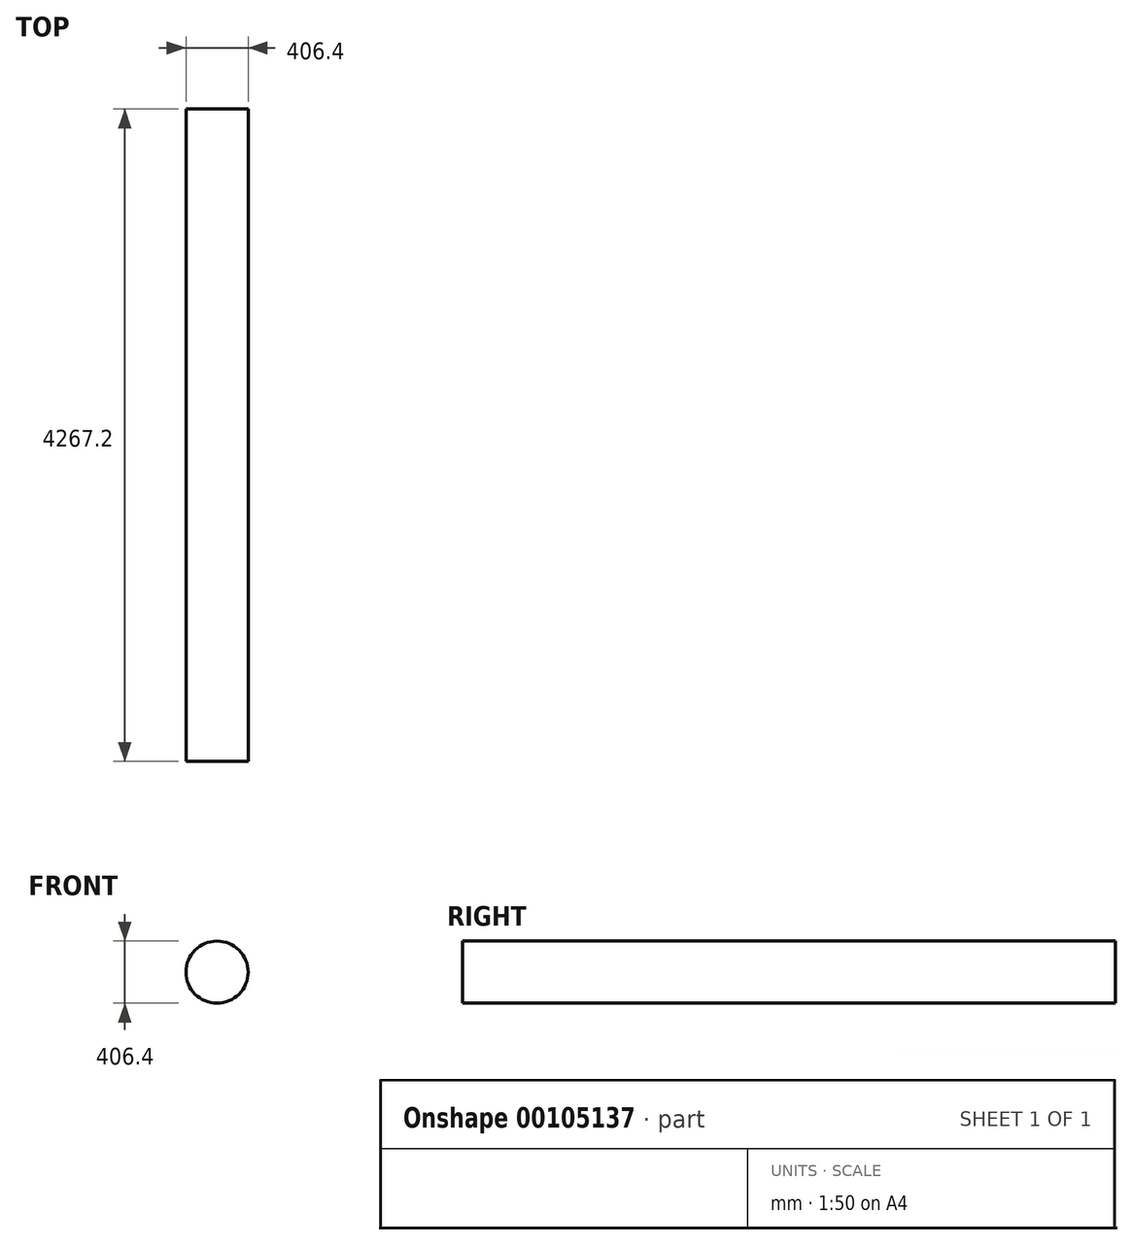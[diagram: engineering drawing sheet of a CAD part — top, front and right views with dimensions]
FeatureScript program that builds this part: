
annotation { "Feature Type Name" : "Feature", "Feature Type Description" : "" }
export const myFeature = defineFeature(function(context is Context, id is Id, definition is map)
    precondition{}
    {
        {
            var Q0;
            Q0=qCreatedBy(makeId("Front.planeOp"),FACE);
            var sketch = newSketch(context, id + "F0", { "sketchPlane" : qUnion([Q0])});
            skCircle(sketch, "E0", {"center": v(0, 0) * mm, "radius": 203.2 * mm});
            skSolve(sketch);
        }
        {
            var Q0;
            Q0=makeQuery(id+"F0.imprint","IMPRINT",FACE,{"disambiguationData":[TD([[makeQuery(id+"F0.imprint","IMPRINT",EDGE,{"derivedFrom":sQuery(id+"F0.wireOp",EDGE,"E0")}),1.0]])]});
            extrude(context, id + "F1", {"entities" : qUnion([Q0]), "depth" : 4267.2 * mm});
        }
    });
